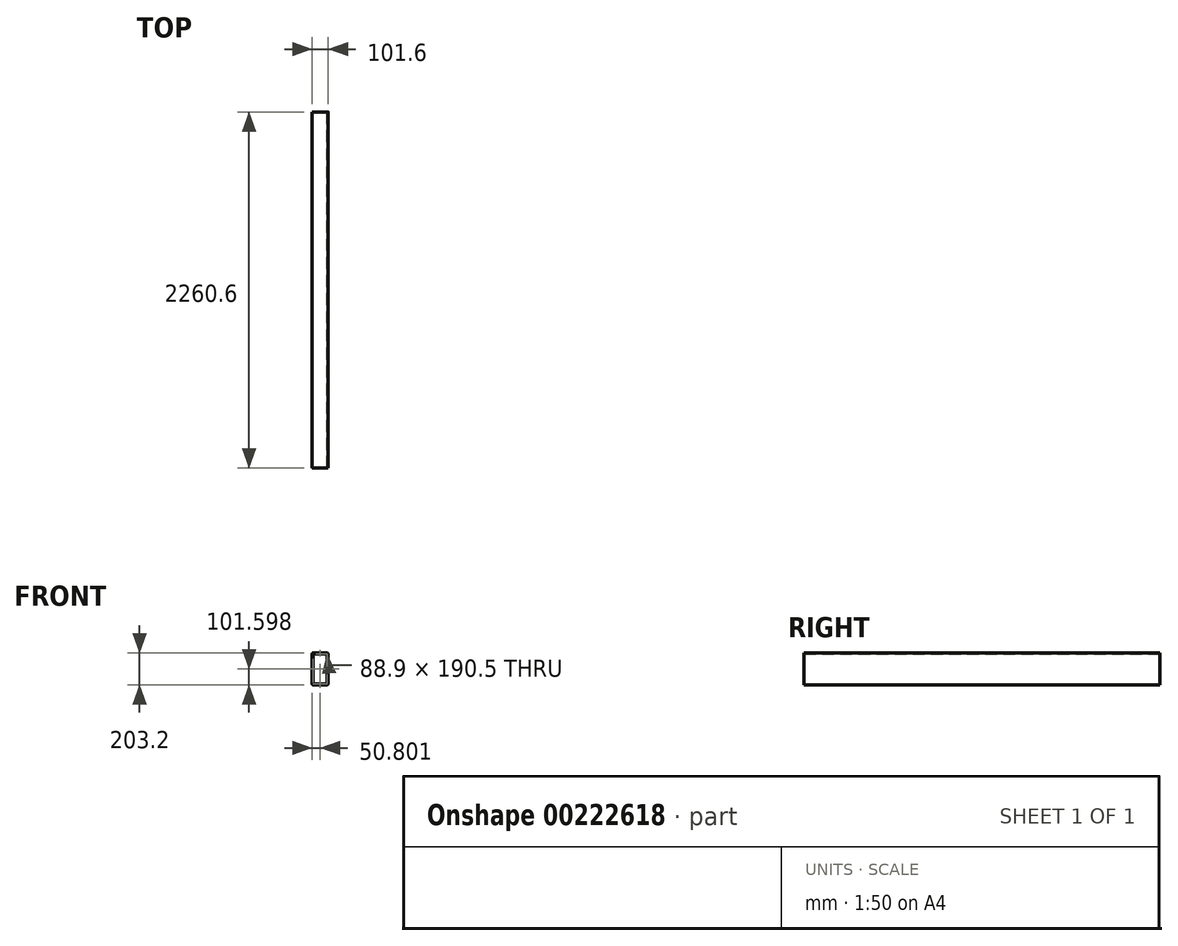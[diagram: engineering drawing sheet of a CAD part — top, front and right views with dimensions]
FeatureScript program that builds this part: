
annotation { "Feature Type Name" : "Feature", "Feature Type Description" : "" }
export const myFeature = defineFeature(function(context is Context, id is Id, definition is map)
    precondition{}
    {
        {
            var Q0;
            Q0=qCreatedBy(makeId("Front.planeOp"),FACE);
            var sketch = newSketch(context, id + "F0", { "sketchPlane" : qUnion([Q0])});
            skLineSegment(sketch, "E0.bottom", {"start": v(-46.6, 102.16) * mm, "end": v(42.3, 102.16) * mm});
            skLineSegment(sketch, "E0.top", {"start": v(-46.6, -101.04) * mm, "end": v(42.3, -101.04) * mm});
            skLineSegment(sketch, "E0.left", {"start": v(-52.95, 95.8) * mm, "end": v(-52.95, -94.7) * mm});
            skLineSegment(sketch, "E0.right", {"start": v(48.65, 95.8) * mm, "end": v(48.65, -94.7) * mm});
            skPoint(sketch, "E1.visualSharp", {"position": v(-52.95, 102.16) * mm});
            skArc(sketch, "E1.filletArc", {"start": v(-46.6, 102.16) * mm, "mid": v(-51.09, 100.3) * mm, "end": v(-52.95, 95.8) * mm});
            skPoint(sketch, "E2.visualSharp", {"position": v(48.65, 102.16) * mm});
            skArc(sketch, "E2.filletArc", {"start": v(48.65, 95.8) * mm, "mid": v(46.8, 100.3) * mm, "end": v(42.3, 102.16) * mm});
            skPoint(sketch, "E3.visualSharp", {"position": v(48.65, -101.04) * mm});
            skArc(sketch, "E3.filletArc", {"start": v(42.3, -101.04) * mm, "mid": v(46.8, -99.18) * mm, "end": v(48.65, -94.7) * mm});
            skPoint(sketch, "E4.visualSharp", {"position": v(-52.95, -101.04) * mm});
            skArc(sketch, "E4.filletArc", {"start": v(-52.95, -94.7) * mm, "mid": v(-51.09, -99.18) * mm, "end": v(-46.6, -101.04) * mm});
            skLineSegment(sketch, "E5.0", {"start": v(-46.6, 95.8) * mm, "end": v(42.3, 95.8) * mm});
            skLineSegment(sketch, "E5.1", {"start": v(-46.6, 95.8) * mm, "end": v(-46.6, -94.7) * mm});
            skLineSegment(sketch, "E5.2", {"start": v(-46.6, -94.7) * mm, "end": v(42.3, -94.7) * mm});
            skLineSegment(sketch, "E5.3", {"start": v(42.3, 95.8) * mm, "end": v(42.3, -94.7) * mm});
            skSolve(sketch);
        }
        {
            var Q0;
            Q0 = qSketchRegion(id + "F0", true);
            extrude(context, id + "F1", {"entities" : qUnion([Q0]), "depth" : 2260.6 * mm});
        }
    });
